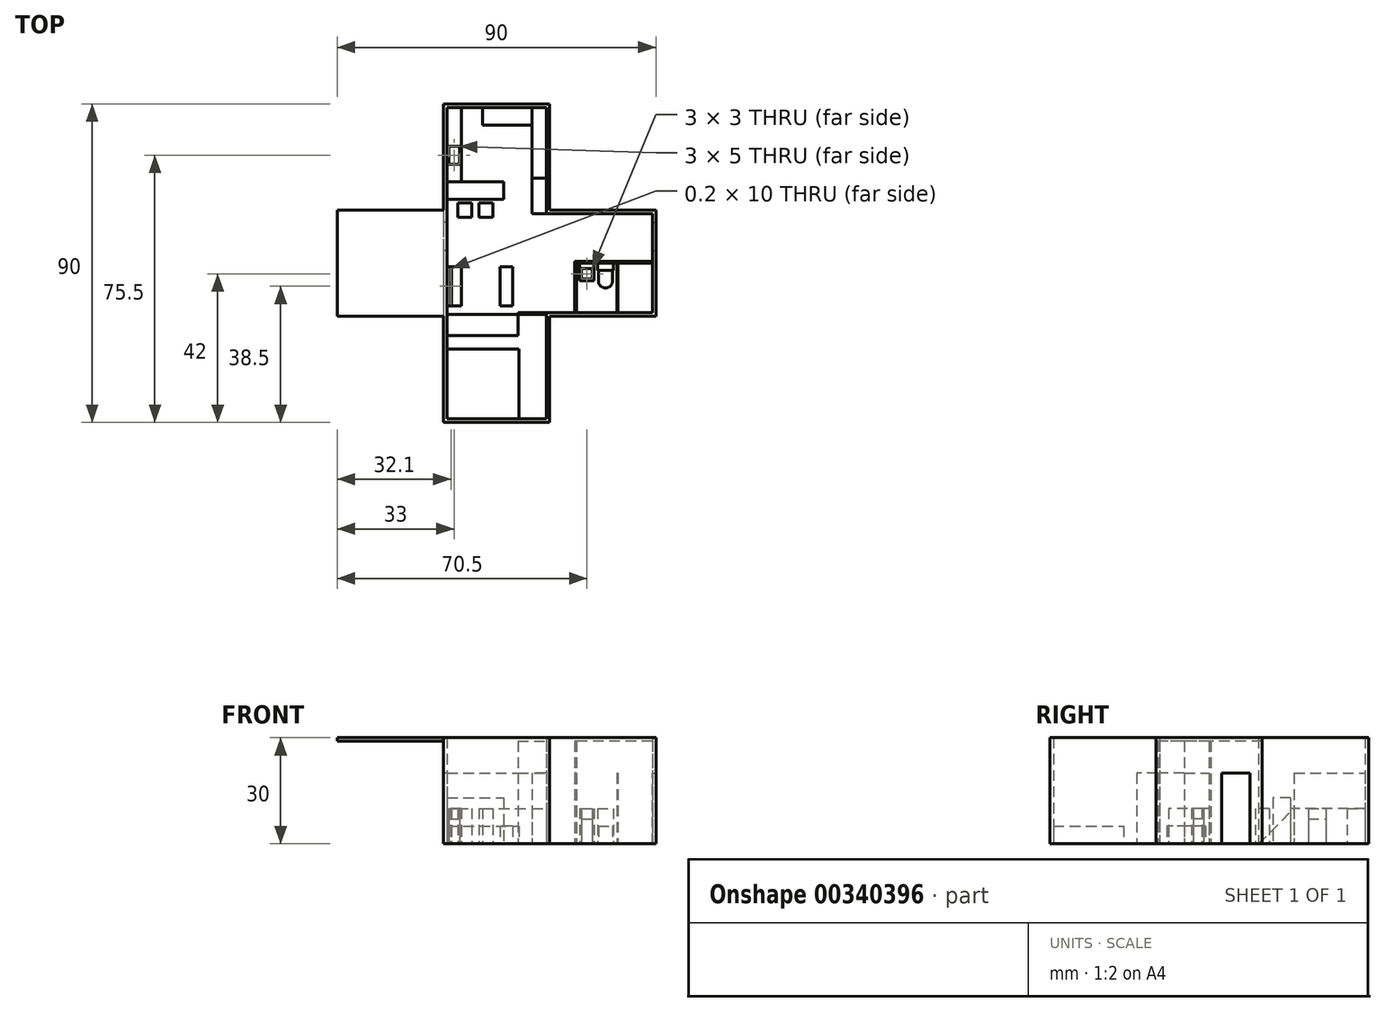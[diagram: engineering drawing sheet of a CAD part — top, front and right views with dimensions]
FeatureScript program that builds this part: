
annotation { "Feature Type Name" : "Feature", "Feature Type Description" : "" }
export const myFeature = defineFeature(function(context is Context, id is Id, definition is map)
    precondition{}
    {
        {
            var Q0;
            Q0=qCreatedBy(makeId("Top.planeOp"),FACE);
            var sketch = newSketch(context, id + "F0", { "sketchPlane" : qUnion([Q0])});
            skLineSegment(sketch, "E0", {"start": v(-15, 45) * mm, "end": v(15, 45) * mm});
            skLineSegment(sketch, "E1", {"start": v(15, 45) * mm, "end": v(15, 15) * mm});
            skLineSegment(sketch, "E2", {"start": v(15, 15) * mm, "end": v(45, 15) * mm});
            skLineSegment(sketch, "E3", {"start": v(45, 15) * mm, "end": v(45, -15) * mm});
            skLineSegment(sketch, "E4", {"start": v(45, -15) * mm, "end": v(15, -15) * mm});
            skLineSegment(sketch, "E5", {"start": v(15, -15) * mm, "end": v(15, -45) * mm});
            skLineSegment(sketch, "E6", {"start": v(15, -45) * mm, "end": v(-15, -45) * mm});
            skLineSegment(sketch, "E7", {"start": v(-45, 0) * mm, "end": v(45, 0) * mm, "construction": true});
            skLineSegment(sketch, "E8", {"start": v(0, -45) * mm, "end": v(0, 45) * mm, "construction": true});
            skLineSegment(sketch, "E9", {"start": v(-15, 45) * mm, "end": v(-15, -45) * mm});
            skSolve(sketch);
        }
        {
            var Q0;
            Q0=makeQuery(id+"F0.imprint","IMPRINT",FACE,{"disambiguationData":[TD([[makeQuery(id+"F0.imprint","IMPRINT",EDGE,{"derivedFrom":sQuery(id+"F0.wireOp",EDGE,"E0")}),-1.0]])]});
            extrude(context, id + "F1", {"entities" : qUnion([Q0]), "depth" : 30 * mm});
        }
        {
            var Q0;
            Q0=makeQuery(id+"F1.opExtrude","CAP_FACE",FACE,{"disambiguationData":[OSD([sQuery(id+"F0.wireOp",EDGE,"E0"),sQuery(id+"F0.wireOp",EDGE,"E1"),sQuery(id+"F0.wireOp",EDGE,"E2"),sQuery(id+"F0.wireOp",EDGE,"E3"),sQuery(id+"F0.wireOp",EDGE,"E4"),sQuery(id+"F0.wireOp",EDGE,"E5"),sQuery(id+"F0.wireOp",EDGE,"E6"),sQuery(id+"F0.wireOp",EDGE,"79uqli7J-U36G-5mOt-l8W7-bvZRfAZijfIB"),sQuery(id+"F0.wireOp",EDGE,"BToaOhAL-iaNv-LXi5-ESiF-BcLewD0NKMmh"),sQuery(id+"F0.wireOp",EDGE,"NxWsr7w1-U29T-vwWz-aLzp-lUtiMVPrrQbN"),sQuery(id+"F0.wireOp",EDGE,"C4ANvElt-fbf8-Z7Ib-7wZb-zL3EDJP0npU2"),sQuery(id+"F0.wireOp",EDGE,"Ylxzn3zR-kqcx-ZaPc-XTMi-K9jEHQCsuisN")])],"isStart":false});
            var Q1;
            Q1=makeQuery(id+"F1.opExtrude","CAP_FACE",FACE,{"disambiguationData":[OSD([sQuery(id+"F0.wireOp",EDGE,"E0"),sQuery(id+"F0.wireOp",EDGE,"E1"),sQuery(id+"F0.wireOp",EDGE,"E2"),sQuery(id+"F0.wireOp",EDGE,"E3"),sQuery(id+"F0.wireOp",EDGE,"E4"),sQuery(id+"F0.wireOp",EDGE,"E5"),sQuery(id+"F0.wireOp",EDGE,"E6"),sQuery(id+"F0.wireOp",EDGE,"79uqli7J-U36G-5mOt-l8W7-bvZRfAZijfIB"),sQuery(id+"F0.wireOp",EDGE,"BToaOhAL-iaNv-LXi5-ESiF-BcLewD0NKMmh"),sQuery(id+"F0.wireOp",EDGE,"NxWsr7w1-U29T-vwWz-aLzp-lUtiMVPrrQbN"),sQuery(id+"F0.wireOp",EDGE,"C4ANvElt-fbf8-Z7Ib-7wZb-zL3EDJP0npU2"),sQuery(id+"F0.wireOp",EDGE,"Ylxzn3zR-kqcx-ZaPc-XTMi-K9jEHQCsuisN")])],"isStart":true});
            shell(context, id + "F2", {"entities" : qUnion([Q0, Q1]), "thickness" : 1 * mm});
        }
        {
            var Q0;
            Q0=qCreatedBy(makeId("Top.planeOp"),FACE);
            var sketch = newSketch(context, id + "F3", { "sketchPlane" : qUnion([Q0])});
            skLineSegment(sketch, "E10.bottom", {"start": v(-14, -14.5) * mm, "end": v(6, -14.5) * mm});
            skLineSegment(sketch, "E10.top", {"start": v(-14, -20.5) * mm, "end": v(6, -20.5) * mm});
            skLineSegment(sketch, "E10.left", {"start": v(-14, -14.5) * mm, "end": v(-14, -20.5) * mm});
            skLineSegment(sketch, "E10.right", {"start": v(6, -14.5) * mm, "end": v(6, -20.5) * mm});
            skLineSegment(sketch, "E11.bottom", {"start": v(44, -14) * mm, "end": v(34, -14) * mm});
            skLineSegment(sketch, "E11.top", {"start": v(44, 0) * mm, "end": v(34, 0) * mm});
            skLineSegment(sketch, "E11.left", {"start": v(44, -14) * mm, "end": v(44, 0) * mm});
            skLineSegment(sketch, "E11.right", {"start": v(34, -14) * mm, "end": v(34, 0) * mm});
            skPoint(sketch, "E12.oppositeSnap0", {"position": v(34, -7) * mm});
            skLineSegment(sketch, "E13.bottom", {"start": v(23.5, 0) * mm, "end": v(27.5, 0) * mm});
            skLineSegment(sketch, "E13.top", {"start": v(23.5, -5) * mm, "end": v(27.5, -5) * mm});
            skLineSegment(sketch, "E13.left", {"start": v(23.5, 0) * mm, "end": v(23.5, -5) * mm});
            skLineSegment(sketch, "E13.right", {"start": v(27.5, 0) * mm, "end": v(27.5, -5) * mm});
            skLineSegment(sketch, "E14.bottom", {"start": v(24, -1.5) * mm, "end": v(27, -1.5) * mm});
            skLineSegment(sketch, "E14.top", {"start": v(24, -4.5) * mm, "end": v(27, -4.5) * mm});
            skLineSegment(sketch, "E14.left", {"start": v(24, -1.5) * mm, "end": v(24, -4.5) * mm});
            skLineSegment(sketch, "E14.right", {"start": v(27, -1.5) * mm, "end": v(27, -4.5) * mm});
            skLineSegment(sketch, "E15.bottom", {"start": v(28.5, 0) * mm, "end": v(33, 0) * mm});
            skLineSegment(sketch, "E15.top", {"start": v(28.5, -2) * mm, "end": v(33, -2) * mm});
            skLineSegment(sketch, "E15.left", {"start": v(28.5, 0) * mm, "end": v(28.5, -2) * mm});
            skLineSegment(sketch, "E15.right", {"start": v(33, 0) * mm, "end": v(33, -2) * mm});
            skLineSegment(sketch, "E16", {"start": v(28.75, -2) * mm, "end": v(28.75, -5) * mm});
            skLineSegment(sketch, "E17", {"start": v(32.75, -2) * mm, "end": v(32.75, -5) * mm});
            skArc(sketch, "E18", {"start": v(28.75, -5) * mm, "mid": v(30.75, -7) * mm, "end": v(32.75, -5) * mm});
            skLineSegment(sketch, "E19", {"start": v(28.75, -5) * mm, "end": v(32.75, -5) * mm, "construction": true});
            skLineSegment(sketch, "E20", {"start": v(44, 0) * mm, "end": v(22.5, 0) * mm});
            skLineSegment(sketch, "E21", {"start": v(22.5, 0) * mm, "end": v(22.5, -14) * mm});
            skLineSegment(sketch, "E22", {"start": v(34.2, 0) * mm, "end": v(34.2, -14) * mm});
            skLineSegment(sketch, "E23", {"start": v(34, -7) * mm, "end": v(34.2, -7) * mm});
            skLineSegment(sketch, "E24", {"start": v(44, 0.5) * mm, "end": v(22, 0.5) * mm});
            skLineSegment(sketch, "E25", {"start": v(22, 0.5) * mm, "end": v(22, -14) * mm});
            skLineSegment(sketch, "E26", {"start": v(22.5, -7) * mm, "end": v(22, -7) * mm});
            skLineSegment(sketch, "E27", {"start": v(6, -14) * mm, "end": v(14, -14) * mm});
            skLineSegment(sketch, "E28", {"start": v(14, -14) * mm, "end": v(14, -14.5) * mm});
            skLineSegment(sketch, "E29", {"start": v(14, -14.5) * mm, "end": v(6, -14.5) * mm});
            skLineSegment(sketch, "E30", {"start": v(6, -14.5) * mm, "end": v(6, -14) * mm});
            skLineSegment(sketch, "E31.bottom", {"start": v(6, -14.5) * mm, "end": v(-14, -14.5) * mm});
            skLineSegment(sketch, "E31.top", {"start": v(6, -14) * mm, "end": v(-14, -14) * mm});
            skLineSegment(sketch, "E31.right", {"start": v(-14, -14.5) * mm, "end": v(-14, -14) * mm});
            skLineSegment(sketch, "E32.top", {"start": v(14, 44) * mm, "end": v(10, 44) * mm});
            skLineSegment(sketch, "E32.left", {"start": v(14, 14) * mm, "end": v(14, 44) * mm});
            skLineSegment(sketch, "E32.right", {"start": v(10, 14) * mm, "end": v(10, 44) * mm});
            skLineSegment(sketch, "E33.bottom", {"start": v(-10, 44) * mm, "end": v(10, 44) * mm});
            skLineSegment(sketch, "E33.top", {"start": v(-10, 39) * mm, "end": v(10, 39) * mm});
            skLineSegment(sketch, "E33.right", {"start": v(10, 44) * mm, "end": v(10, 39) * mm});
            skLineSegment(sketch, "E34.bottom", {"start": v(-10, 44) * mm, "end": v(-14, 44) * mm});
            skLineSegment(sketch, "E34.top", {"start": v(-10, 23) * mm, "end": v(-14, 23) * mm});
            skLineSegment(sketch, "E34.left", {"start": v(-10, 39) * mm, "end": v(-10, 23) * mm});
            skLineSegment(sketch, "E34.right", {"start": v(-14, 44) * mm, "end": v(-14, 23) * mm});
            skLineSegment(sketch, "E35.bottom", {"start": v(-14, 23) * mm, "end": v(2, 23) * mm});
            skLineSegment(sketch, "E35.top", {"start": v(-14, 18) * mm, "end": v(2, 18) * mm});
            skLineSegment(sketch, "E35.left", {"start": v(-14, 23) * mm, "end": v(-14, 18) * mm});
            skLineSegment(sketch, "E35.right", {"start": v(2, 23) * mm, "end": v(2, 18) * mm});
            skLineSegment(sketch, "E36", {"start": v(10, 14) * mm, "end": v(14, 14) * mm});
            skLineSegment(sketch, "E37.bottom", {"start": v(-11, 17) * mm, "end": v(-7, 17) * mm});
            skLineSegment(sketch, "E37.top", {"start": v(-11, 13) * mm, "end": v(-7, 13) * mm});
            skLineSegment(sketch, "E37.left", {"start": v(-11, 17) * mm, "end": v(-11, 13) * mm});
            skLineSegment(sketch, "E37.right", {"start": v(-7, 17) * mm, "end": v(-7, 13) * mm});
            skLineSegment(sketch, "E38.bottom", {"start": v(-5, 17) * mm, "end": v(-1, 17) * mm});
            skLineSegment(sketch, "E38.top", {"start": v(-5, 13) * mm, "end": v(-1, 13) * mm});
            skLineSegment(sketch, "E38.left", {"start": v(-5, 17) * mm, "end": v(-5, 13) * mm});
            skLineSegment(sketch, "E38.right", {"start": v(-1, 17) * mm, "end": v(-1, 13) * mm});
            skLineSegment(sketch, "E39.bottom", {"start": v(-14, -1) * mm, "end": v(-10, -1) * mm});
            skLineSegment(sketch, "E39.top", {"start": v(-14, -12) * mm, "end": v(-10, -12) * mm});
            skLineSegment(sketch, "E39.left", {"start": v(-14, -1) * mm, "end": v(-14, -12) * mm});
            skLineSegment(sketch, "E39.right", {"start": v(-10, -1) * mm, "end": v(-10, -12) * mm});
            skLineSegment(sketch, "E40.bottom", {"start": v(-13, -1.5) * mm, "end": v(-12.8, -1.5) * mm});
            skLineSegment(sketch, "E40.top", {"start": v(-13, -11.5) * mm, "end": v(-12.8, -11.5) * mm});
            skLineSegment(sketch, "E40.left", {"start": v(-13, -1.5) * mm, "end": v(-13, -11.5) * mm});
            skLineSegment(sketch, "E40.right", {"start": v(-12.8, -1.5) * mm, "end": v(-12.8, -11.5) * mm});
            skLineSegment(sketch, "E41", {"start": v(10, 24) * mm, "end": v(14, 24) * mm});
            skLineSegment(sketch, "E42.bottom", {"start": v(1, -14) * mm, "end": v(6, -14) * mm});
            skLineSegment(sketch, "E42.top", {"start": v(1, 1) * mm, "end": v(6, 1) * mm});
            skLineSegment(sketch, "E42.left", {"start": v(1, -14) * mm, "end": v(1, 1) * mm});
            skLineSegment(sketch, "E42.right", {"start": v(6, -14) * mm, "end": v(6, 1) * mm});
            skLineSegment(sketch, "E43.bottom", {"start": v(-14, -44) * mm, "end": v(6.3, -44) * mm});
            skLineSegment(sketch, "E43.top", {"start": v(-14, -24.2) * mm, "end": v(6.3, -24.2) * mm});
            skLineSegment(sketch, "E43.left", {"start": v(-14, -44) * mm, "end": v(-14, -24.2) * mm});
            skLineSegment(sketch, "E43.right", {"start": v(6.3, -44) * mm, "end": v(6.3, -24.2) * mm});
            skLineSegment(sketch, "E44", {"start": v(44, 0.5) * mm, "end": v(44, 0) * mm});
            skLineSegment(sketch, "E45", {"start": v(22.5, 0) * mm, "end": v(22, 0) * mm});
            skLineSegment(sketch, "E46", {"start": v(22, -14) * mm, "end": v(22.5, -14) * mm});
            skLineSegment(sketch, "E47", {"start": v(-14, -14) * mm, "end": v(-14, -14.5) * mm});
            skLineSegment(sketch, "E48.bottom", {"start": v(4.5, -1) * mm, "end": v(1, -1) * mm});
            skLineSegment(sketch, "E48.top", {"start": v(4.5, -12) * mm, "end": v(1, -12) * mm});
            skLineSegment(sketch, "E48.left", {"start": v(4.5, -1) * mm, "end": v(4.5, -12) * mm});
            skLineSegment(sketch, "E48.right", {"start": v(1, -1) * mm, "end": v(1, -12) * mm});
            skLineSegment(sketch, "E49", {"start": v(6, -6.5) * mm, "end": v(-14, -6.5) * mm, "construction": true});
            skLineSegment(sketch, "E50", {"start": v(-10, -6.5) * mm, "end": v(-14, -6.5) * mm, "construction": true});
            skLineSegment(sketch, "E51.bottom", {"start": v(-13.5, 28) * mm, "end": v(-10.5, 28) * mm});
            skLineSegment(sketch, "E51.top", {"start": v(-13.5, 33) * mm, "end": v(-10.5, 33) * mm});
            skLineSegment(sketch, "E51.left", {"start": v(-13.5, 28) * mm, "end": v(-13.5, 33) * mm});
            skLineSegment(sketch, "E51.right", {"start": v(-10.5, 28) * mm, "end": v(-10.5, 33) * mm});
            skLineSegment(sketch, "E52.bottom", {"start": v(-10, 39) * mm, "end": v(-4, 39) * mm});
            skLineSegment(sketch, "E52.top", {"start": v(-10, 44) * mm, "end": v(-4, 44) * mm});
            skLineSegment(sketch, "E52.left", {"start": v(-10, 39) * mm, "end": v(-10, 44) * mm});
            skLineSegment(sketch, "E52.right", {"start": v(-4, 39) * mm, "end": v(-4, 44) * mm});
            skLineSegment(sketch, "E53", {"start": v(-10, 41.5) * mm, "end": v(-4, 41.5) * mm, "construction": true});
            skLineSegment(sketch, "E54", {"start": v(-7, 39) * mm, "end": v(-7, 44) * mm, "construction": true});
            skLineSegment(sketch, "E55", {"start": v(-10, 44) * mm, "end": v(-4, 39) * mm, "construction": true});
            skLineSegment(sketch, "E56", {"start": v(-4, 44) * mm, "end": v(-10, 39) * mm, "construction": true});
            skLineSegment(sketch, "E57", {"start": v(-7, 39) * mm, "end": v(-10, 41.5) * mm, "construction": true});
            skLineSegment(sketch, "E58", {"start": v(-4, 41.5) * mm, "end": v(-7, 44) * mm, "construction": true});
            skLineSegment(sketch, "E59", {"start": v(-7, 44) * mm, "end": v(-10, 41.5) * mm, "construction": true});
            skLineSegment(sketch, "E60", {"start": v(-7, 39) * mm, "end": v(-4, 41.5) * mm, "construction": true});
            skCircle(sketch, "E61", {"center": v(-8.5, 42.75) * mm, "radius": 0.88 * mm});
            skCircle(sketch, "E62", {"center": v(-5.5, 42.75) * mm, "radius": 0.88 * mm});
            skCircle(sketch, "E63", {"center": v(-5.5, 40.25) * mm, "radius": 0.88 * mm});
            skCircle(sketch, "E64", {"center": v(-8.5, 40.25) * mm, "radius": 0.88 * mm});
            skSolve(sketch);
        }
        {
            var Q0;
            Q0=qCreatedBy(makeId("Top.planeOp"),FACE);
            var sketch = newSketch(context, id + "F4", { "sketchPlane" : qUnion([Q0])});
            skLineSegment(sketch, "E65", {"start": v(-15, 15) * mm, "end": v(-15, 45) * mm});
            skLineSegment(sketch, "E66", {"start": v(-15, 45) * mm, "end": v(15, 45) * mm});
            skLineSegment(sketch, "E67", {"start": v(15, 45) * mm, "end": v(15, 15) * mm});
            skLineSegment(sketch, "E68", {"start": v(15, 15) * mm, "end": v(45, 15) * mm});
            skLineSegment(sketch, "E69", {"start": v(45, 15) * mm, "end": v(45, -15) * mm});
            skLineSegment(sketch, "E70", {"start": v(45, -15) * mm, "end": v(15, -15) * mm});
            skLineSegment(sketch, "E71", {"start": v(15, -15) * mm, "end": v(15, -45) * mm});
            skLineSegment(sketch, "E72", {"start": v(15, -45) * mm, "end": v(-15, -45) * mm});
            skLineSegment(sketch, "E73", {"start": v(-15, -45) * mm, "end": v(-15, -15) * mm});
            skLineSegment(sketch, "E74", {"start": v(-15, -15) * mm, "end": v(-45, -15) * mm});
            skLineSegment(sketch, "E75", {"start": v(-45, -15) * mm, "end": v(-45, 15) * mm});
            skLineSegment(sketch, "E76", {"start": v(-45, 15) * mm, "end": v(-15, 15) * mm});
            skSolve(sketch);
        }
        {
            var Q0;
            Q0=makeQuery(id+"F1.opExtrude","SWEPT_FACE",FACE,{"disambiguationData":[OSD([sQuery(id+"F0.wireOp",EDGE,"E3")])]});
            var sketch = newSketch(context, id + "F5", { "sketchPlane" : qUnion([Q0])});
            skLineSegment(sketch, "E77.bottom", {"start": v(3.5, 0) * mm, "end": v(11.5, 0) * mm});
            skLineSegment(sketch, "E77.top", {"start": v(3.5, 20) * mm, "end": v(11.5, 20) * mm});
            skLineSegment(sketch, "E77.left", {"start": v(3.5, 0) * mm, "end": v(3.5, 20) * mm});
            skLineSegment(sketch, "E77.right", {"start": v(11.5, 0) * mm, "end": v(11.5, 20) * mm});
            skSolve(sketch);
        }
        {
            var Q0;
            Q0=makeQuery(id+"F1.opExtrude","SWEPT_FACE",FACE,{"disambiguationData":[OSD([sQuery(id+"F0.wireOp",EDGE,"E9")])]});
            var sketch = newSketch(context, id + "F6", { "sketchPlane" : qUnion([Q0])});
            skLineSegment(sketch, "E78.bottom", {"start": v(-11.5, 20) * mm, "end": v(-3.5, 20) * mm});
            skLineSegment(sketch, "E78.top", {"start": v(-11.5, 0) * mm, "end": v(-3.5, 0) * mm});
            skLineSegment(sketch, "E78.left", {"start": v(-11.5, 20) * mm, "end": v(-11.5, 0) * mm});
            skLineSegment(sketch, "E78.right", {"start": v(-3.5, 20) * mm, "end": v(-3.5, 0) * mm});
            skSolve(sketch);
        }
        {
            var Q0;
            Q0 = qSketchRegion(id + "F5", true);
            extrude(context, id + "F7", {"entities" : qUnion([Q0]), "operationType" : NewBodyOperationType.REMOVE, "oppositeDirection" : true, "depth" : 1 * mm});
        }
        {
            var Q0;
            Q0 = qSketchRegion(id + "F5", true);
            extrude(context, id + "F8", {"entities" : qUnion([Q0]), "oppositeDirection" : true, "depth" : 1 * mm});
        }
        {
            var Q0;
            Q0 = qSketchRegion(id + "F6", true);
            extrude(context, id + "F9", {"entities" : qUnion([Q0]), "operationType" : NewBodyOperationType.REMOVE, "oppositeDirection" : true, "depth" : 1 * mm});
        }
        {
            var Q0;
            Q0 = qSketchRegion(id + "F6", true);
            extrude(context, id + "F10", {"entities" : qUnion([Q0]), "oppositeDirection" : true, "depth" : 1 * mm});
        }
        {
            var Q0;
            {var subQ5=sQuery(id+"F3.wireOp",EDGE,"E23");Q0=makeQuery(id+"F3.imprint","IMPRINT",FACE,{"disambiguationData":[TD([[makeQuery(id+"F3.imprint","IMPRINT",EDGE,{"derivedFrom":subQ5}),-1.0]])]});}
            var Q1;
            Q1=makeQuery(id+"F3.imprint","IMPRINT",FACE,{"disambiguationData":[TD([[makeQuery(id+"F3.imprint","IMPRINT",EDGE,{"derivedFrom":sQuery(id+"F3.wireOp",EDGE,"E10.top")}),1.0]])]});
            var Q2;
            {var subQ4=sQuery(id+"F3.wireOp",EDGE,"E32.top");Q2=makeQuery(id+"F3.imprint","IMPRINT",FACE,{"disambiguationData":[TD([[makeQuery(id+"F3.imprint","IMPRINT",EDGE,{"derivedFrom":subQ4}),1.0]])]});}
            extrude(context, id + "F11", {"entities" : qUnion([Q0, Q1, Q2]), "depth" : 20 * mm});
        }
        {
            var Q0;
            Q0=makeQuery(id+"F3.imprint","IMPRINT",FACE,{"disambiguationData":[TD([[makeQuery(id+"F3.imprint","IMPRINT",EDGE,{"derivedFrom":sQuery(id+"F3.wireOp",EDGE,"E31.bottom")}),-1.0]])]});
            var Q1;
            {var subQ2=sQuery(id+"F3.wireOp",EDGE,"E26");Q1=makeQuery(id+"F3.imprint","IMPRINT",FACE,{"disambiguationData":[TD([[makeQuery(id+"F3.imprint","IMPRINT",EDGE,{"derivedFrom":subQ2}),-1.0]])]});}
            var Q2;
            {var subQ7=sQuery(id+"F3.wireOp",EDGE,"E24");Q2=makeQuery(id+"F3.imprint","IMPRINT",FACE,{"disambiguationData":[TD([[makeQuery(id+"F3.imprint","IMPRINT",EDGE,{"derivedFrom":subQ7}),1.0]])]});}
            extrude(context, id + "F12", {"entities" : qUnion([Q0, Q1, Q2]), "depth" : 29 * mm});
        }
        {
            var Q0;
            Q0=makeQuery(id+"F3.imprint","IMPRINT",FACE,{"disambiguationData":[TD([[makeQuery(id+"F3.imprint","IMPRINT",EDGE,{"derivedFrom":sQuery(id+"F3.wireOp",EDGE,"E27")}),-1.0]])]});
            var Q1;
            {var subQ2=sQuery(id+"F3.wireOp",EDGE,"E26");Q1=makeQuery(id+"F3.imprint","IMPRINT",FACE,{"disambiguationData":[TD([[makeQuery(id+"F3.imprint","IMPRINT",EDGE,{"derivedFrom":subQ2}),1.0]])]});}
            extrude(context, id + "F13", {"entities" : qUnion([Q0, Q1]), "depth" : 29 * mm});
        }
        {
            var Q0;
            Q0=makeQuery(id+"F3.imprint","IMPRINT",FACE,{"disambiguationData":[TD([[makeQuery(id+"F3.imprint","IMPRINT",EDGE,{"derivedFrom":sQuery(id+"F3.wireOp",EDGE,"E27")}),-1.0]])]});
            var Q1;
            {var subQ2=sQuery(id+"F3.wireOp",EDGE,"E26");Q1=makeQuery(id+"F3.imprint","IMPRINT",FACE,{"disambiguationData":[TD([[makeQuery(id+"F3.imprint","IMPRINT",EDGE,{"derivedFrom":subQ2}),1.0]])]});}
            extrude(context, id + "F14", {"entities" : qUnion([Q0, Q1]), "operationType" : NewBodyOperationType.REMOVE, "depth" : 20 * mm});
        }
        {
            var Q0;
            Q0=makeQuery(id+"F3.imprint","IMPRINT",FACE,{"disambiguationData":[TD([[makeQuery(id+"F3.imprint","IMPRINT",EDGE,{"derivedFrom":sQuery(id+"F3.wireOp",EDGE,"E27")}),-1.0]])]});
            var Q1;
            {var subQ2=sQuery(id+"F3.wireOp",EDGE,"E26");Q1=makeQuery(id+"F3.imprint","IMPRINT",FACE,{"disambiguationData":[TD([[makeQuery(id+"F3.imprint","IMPRINT",EDGE,{"derivedFrom":subQ2}),1.0]])]});}
            extrude(context, id + "F15", {"entities" : qUnion([Q0, Q1]), "depth" : 20 * mm});
        }
        {
            var Q0;
            {var subQ3=sQuery(id+"F3.wireOp",EDGE,"E23");Q0=makeQuery(id+"F3.imprint","IMPRINT",FACE,{"disambiguationData":[TD([[makeQuery(id+"F3.imprint","IMPRINT",EDGE,{"derivedFrom":subQ3}),1.0]])]});}
            extrude(context, id + "F16", {"entities" : qUnion([Q0]), "depth" : 20 * mm});
        }
        {
            var Q0;
            Q0=makeQuery(id+"F3.imprint","IMPRINT",FACE,{"disambiguationData":[TD([[makeQuery(id+"F3.imprint","IMPRINT",EDGE,{"derivedFrom":sQuery(id+"F3.wireOp",EDGE,"E13.top")}),1.0]])]});
            var Q1;
            {var subQ5=sQuery(id+"F3.wireOp",EDGE,"E42.bottom");Q1=makeQuery(id+"F3.imprint","IMPRINT",FACE,{"disambiguationData":[TD([[makeQuery(id+"F3.imprint","IMPRINT",EDGE,{"derivedFrom":subQ5}),1.0]])]});}
            var Q2;
            Q2=makeQuery(id+"F3.imprint","IMPRINT",FACE,{"disambiguationData":[TD([[makeQuery(id+"F3.imprint","IMPRINT",EDGE,{"derivedFrom":sQuery(id+"F3.wireOp",EDGE,"E37.bottom")}),-1.0]])]});
            var Q3;
            Q3=makeQuery(id+"F3.imprint","IMPRINT",FACE,{"disambiguationData":[TD([[makeQuery(id+"F3.imprint","IMPRINT",EDGE,{"derivedFrom":sQuery(id+"F3.wireOp",EDGE,"E38.bottom")}),-1.0]])]});
            var Q4;
            Q4=makeQuery(id+"F3.imprint","IMPRINT",FACE,{"disambiguationData":[TD([[makeQuery(id+"F3.imprint","IMPRINT",EDGE,{"derivedFrom":sQuery(id+"F3.wireOp",EDGE,"E40.bottom")}),-1.0]])]});
            var Q5;
            {var subQ0=sQuery(id+"F3.wireOp",EDGE,"E15.left");Q5=makeQuery(id+"F3.imprint","IMPRINT",FACE,{"disambiguationData":[TD([[makeQuery(id+"F3.imprint","IMPRINT",EDGE,{"derivedFrom":subQ0}),1.0]])]});}
            var Q6;
            Q6=makeQuery(id+"F3.imprint","IMPRINT",FACE,{"disambiguationData":[TD([[makeQuery(id+"F3.imprint","IMPRINT",EDGE,{"derivedFrom":sQuery(id+"F3.wireOp",EDGE,"E34.bottom")}),1.0]])]});
            var Q7;
            Q7=makeQuery(id+"F3.imprint","IMPRINT",FACE,{"disambiguationData":[TD([[makeQuery(id+"F3.imprint","IMPRINT",EDGE,{"derivedFrom":sQuery(id+"F3.wireOp",EDGE,"E33.bottom")}),-1.0]])]});
            var Q8;
            Q8=makeQuery(id+"F3.imprint","IMPRINT",FACE,{"disambiguationData":[TD([[makeQuery(id+"F3.imprint","IMPRINT",EDGE,{"derivedFrom":sQuery(id+"F3.wireOp",EDGE,"E52.bottom")}),1.0]])]});
            extrude(context, id + "F17", {"entities" : qUnion([Q0, Q1, Q2, Q3, Q4, Q5, Q6, Q7, Q8]), "depth" : 10 * mm});
        }
        {
            var Q0;
            {var subQ0=sQuery(id+"F3.wireOp",EDGE,"E16");Q0=makeQuery(id+"F3.imprint","IMPRINT",FACE,{"disambiguationData":[TD([[makeQuery(id+"F3.imprint","IMPRINT",EDGE,{"derivedFrom":subQ0}),1.0]])]});}
            var Q1;
            Q1=makeQuery(id+"F3.imprint","IMPRINT",FACE,{"disambiguationData":[TD([[makeQuery(id+"F3.imprint","IMPRINT",EDGE,{"derivedFrom":sQuery(id+"F3.wireOp",EDGE,"E48.bottom")}),1.0]])]});
            var Q2;
            Q2=makeQuery(id+"F3.imprint","IMPRINT",FACE,{"disambiguationData":[TD([[makeQuery(id+"F3.imprint","IMPRINT",EDGE,{"derivedFrom":sQuery(id+"F3.wireOp",EDGE,"E39.bottom")}),-1.0]])]});
            var Q3;
            Q3=makeQuery(id+"F3.imprint","IMPRINT",FACE,{"disambiguationData":[TD([[makeQuery(id+"F3.imprint","IMPRINT",EDGE,{"derivedFrom":sQuery(id+"F3.wireOp",EDGE,"E43.bottom")}),1.0]])]});
            extrude(context, id + "F18", {"entities" : qUnion([Q0, Q1, Q2, Q3]), "depth" : 5 * mm});
        }
        {
            var Q0;
            Q0=makeQuery(id+"F3.imprint","IMPRINT",FACE,{"disambiguationData":[TD([[makeQuery(id+"F3.imprint","IMPRINT",EDGE,{"derivedFrom":sQuery(id+"F3.wireOp",EDGE,"E14.bottom")}),-1.0]])]});
            var Q1;
            Q1=makeQuery(id+"F3.imprint","IMPRINT",FACE,{"disambiguationData":[TD([[makeQuery(id+"F3.imprint","IMPRINT",EDGE,{"derivedFrom":sQuery(id+"F3.wireOp",EDGE,"E51.bottom")}),1.0]])]});
            extrude(context, id + "F19", {"entities" : qUnion([Q0, Q1]), "depth" : 7 * mm});
        }
        {
            var Q0;
            Q0=makeQuery(id+"F3.imprint","IMPRINT",FACE,{"disambiguationData":[TD([[makeQuery(id+"F3.imprint","IMPRINT",EDGE,{"derivedFrom":sQuery(id+"F3.wireOp",EDGE,"E35.top")}),1.0]])]});
            extrude(context, id + "F20", {"entities" : qUnion([Q0]), "depth" : 13 * mm});
        }
        {
            var Q0;
            Q0=sQuery(id+"F3.wireOp",EDGE,"E63");
            var Q1;
            Q1=sQuery(id+"F3.wireOp",EDGE,"E64");
            var Q2;
            Q2=sQuery(id+"F3.wireOp",EDGE,"E61");
            var Q3;
            Q3=sQuery(id+"F3.wireOp",EDGE,"E62");
            extrude(context, id + "F21", {"bodyType" : ToolBodyType.SURFACE, "surfaceEntities" : qUnion([Q0, Q1, Q2, Q3]), "depth" : 11 * mm});
        }
        {
            var Q0;
            {var subQ0=sQuery(id+"F3.wireOp",EDGE,"E36");Q0=makeQuery(id+"F3.imprint","IMPRINT",FACE,{"disambiguationData":[TD([[makeQuery(id+"F3.imprint","IMPRINT",EDGE,{"derivedFrom":subQ0}),1.0]])]});}
            extrude(context, id + "F22", {"entities" : qUnion([Q0]), "depth" : 15 * mm});
        }
        {
            var Q0;
            Q0=makeQuery(id+"F22.opExtrude","CAP_EDGE",EDGE,{"disambiguationData":[OSD([sQuery(id+"F3.wireOp",EDGE,"E36")])],"isStart":false});
            chamfer(context, id + "F23", {"entities" : qUnion([Q0]), "width" : 15 * mm, "tangentPropagation" : true});
        }
        {
            var Q0;
            Q0=makeQuery(id+"F1.opExtrude","CAP_FACE",FACE,{"disambiguationData":[OSD([sQuery(id+"F0.wireOp",EDGE,"E0"),sQuery(id+"F0.wireOp",EDGE,"E1"),sQuery(id+"F0.wireOp",EDGE,"E2"),sQuery(id+"F0.wireOp",EDGE,"E3"),sQuery(id+"F0.wireOp",EDGE,"E4"),sQuery(id+"F0.wireOp",EDGE,"E5"),sQuery(id+"F0.wireOp",EDGE,"E6"),sQuery(id+"F0.wireOp",EDGE,"E9")])],"isStart":false});
            var sketch = newSketch(context, id + "F24", { "sketchPlane" : qUnion([Q0])});
            skLineSegment(sketch, "E79", {"start": v(-15, 15) * mm, "end": v(-15, 45) * mm});
            skLineSegment(sketch, "E80", {"start": v(-15, 45) * mm, "end": v(15, 45) * mm});
            skLineSegment(sketch, "E81", {"start": v(15, 45) * mm, "end": v(15, 15) * mm});
            skLineSegment(sketch, "E82", {"start": v(15, 15) * mm, "end": v(45, 15) * mm});
            skLineSegment(sketch, "E83", {"start": v(45, 15) * mm, "end": v(45, -15) * mm});
            skLineSegment(sketch, "E84", {"start": v(45, -15) * mm, "end": v(15, -15) * mm});
            skLineSegment(sketch, "E85", {"start": v(15, -15) * mm, "end": v(15, -45) * mm});
            skLineSegment(sketch, "E86", {"start": v(15, -45) * mm, "end": v(-15, -45) * mm});
            skLineSegment(sketch, "E87", {"start": v(-15, -45) * mm, "end": v(-15, -15) * mm});
            skLineSegment(sketch, "E88", {"start": v(-15, -15) * mm, "end": v(-45, -15) * mm});
            skLineSegment(sketch, "E89", {"start": v(-45, -15) * mm, "end": v(-45, 15) * mm});
            skLineSegment(sketch, "E90", {"start": v(-45, 15) * mm, "end": v(-15, 15) * mm});
            skLineSegment(sketch, "E91", {"start": v(-15, -15) * mm, "end": v(-15, 15) * mm});
            skSolve(sketch);
        }
        {
            var Q0;
            Q0=makeQuery(id+"F24.imprint","IMPRINT",FACE,{"disambiguationData":[TD([[makeQuery(id+"F24.imprint","IMPRINT",EDGE,{"derivedFrom":sQuery(id+"F24.wireOp",EDGE,"E88")}),-1.0]])]});
            extrude(context, id + "F25", {"entities" : qUnion([Q0]), "operationType" : NewBodyOperationType.ADD, "oppositeDirection" : true, "depth" : 1 * mm});
        }
    });
